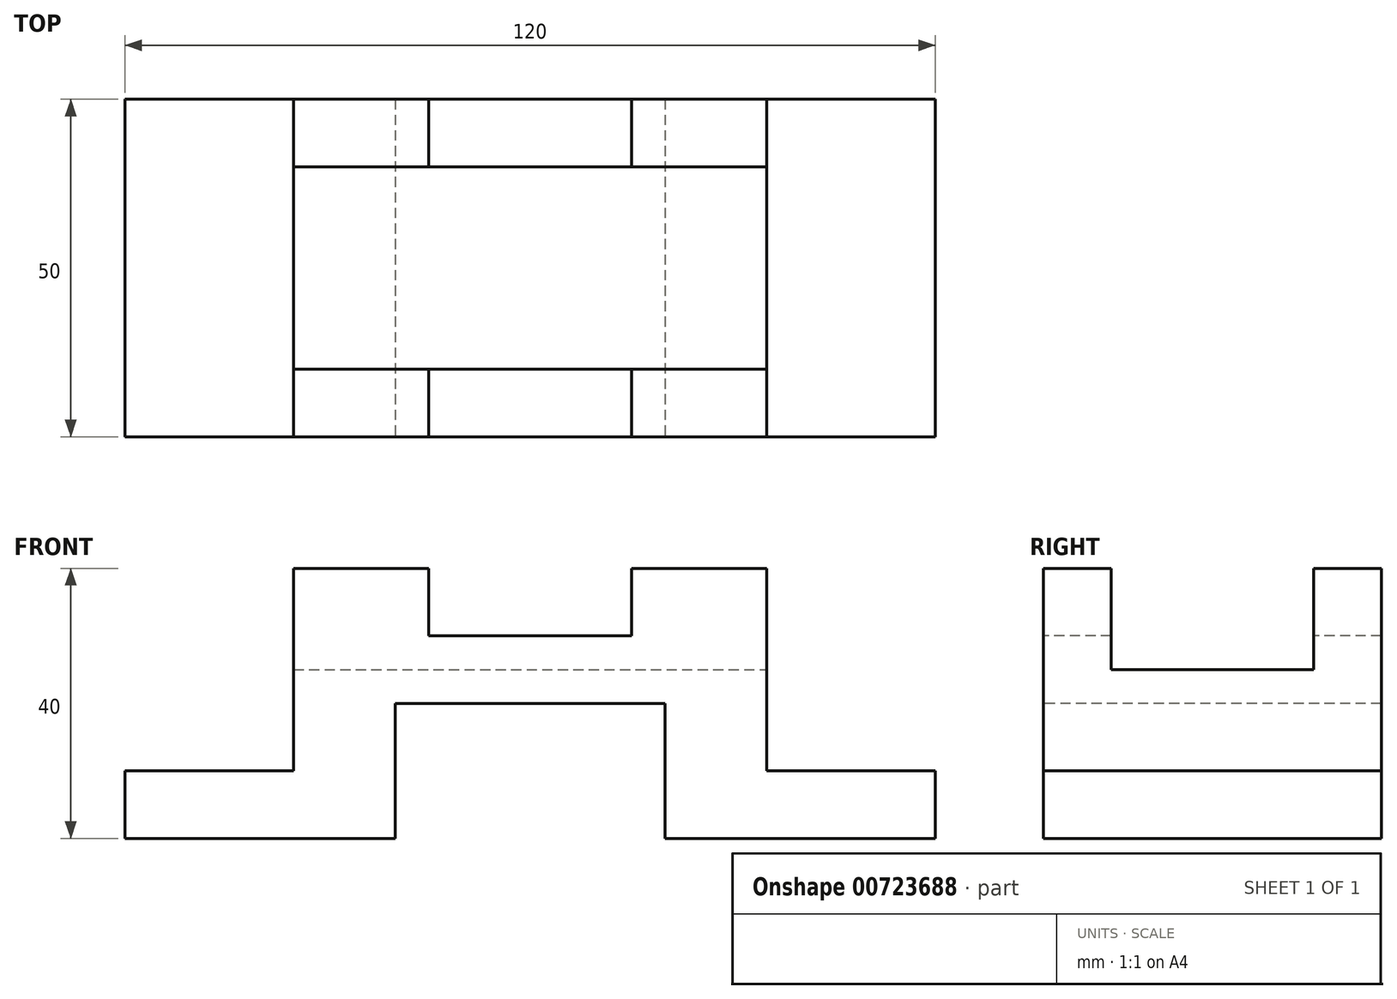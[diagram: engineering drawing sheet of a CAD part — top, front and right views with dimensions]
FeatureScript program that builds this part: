
annotation { "Feature Type Name" : "Feature", "Feature Type Description" : "" }
export const myFeature = defineFeature(function(context is Context, id is Id, definition is map)
    precondition{}
    {
        {
            var Q0;
            Q0=qCreatedBy(makeId("Front.planeOp"),FACE);
            var sketch = newSketch(context, id + "F0", { "sketchPlane" : qUnion([Q0])});
            skLineSegment(sketch, "E0", {"start": v(0, 0) * mm, "end": v(-40, 0) * mm});
            skLineSegment(sketch, "E1", {"start": v(-40, 0) * mm, "end": v(-40, 20) * mm});
            skLineSegment(sketch, "E2", {"start": v(-40, 20) * mm, "end": v(-80, 20) * mm});
            skLineSegment(sketch, "E3", {"start": v(-80, 20) * mm, "end": v(-80, 0) * mm});
            skLineSegment(sketch, "E4", {"start": v(-80, 0) * mm, "end": v(-120, 0) * mm});
            skLineSegment(sketch, "E5", {"start": v(-120, 0) * mm, "end": v(-120, 10) * mm});
            skLineSegment(sketch, "E6", {"start": v(-120, 10) * mm, "end": v(-95, 10) * mm});
            skLineSegment(sketch, "E7", {"start": v(-95, 10) * mm, "end": v(-95, 40) * mm});
            skLineSegment(sketch, "E8", {"start": v(-95, 40) * mm, "end": v(-75, 40) * mm});
            skLineSegment(sketch, "E9", {"start": v(-75, 40) * mm, "end": v(-75, 30) * mm});
            skLineSegment(sketch, "E10", {"start": v(-75, 30) * mm, "end": v(-45, 30) * mm});
            skLineSegment(sketch, "E11", {"start": v(-45, 30) * mm, "end": v(-45, 40) * mm});
            skLineSegment(sketch, "E12", {"start": v(-45, 40) * mm, "end": v(-25, 40) * mm});
            skLineSegment(sketch, "E13", {"start": v(-25, 40) * mm, "end": v(-25, 10) * mm});
            skLineSegment(sketch, "E14", {"start": v(-25, 10) * mm, "end": v(0, 10) * mm});
            skLineSegment(sketch, "E15", {"start": v(0, 10) * mm, "end": v(0, 0) * mm});
            skSolve(sketch);
        }
        {
            var Q0;
            Q0 = qSketchRegion(id + "F0", true);
            extrude(context, id + "F1", {"entities" : qUnion([Q0]), "oppositeDirection" : true, "depth" : 50 * mm, "offsetDistance" : 25 * mm});
        }
        {
            var Q0;
            Q0=makeQuery(id+"F1.opExtrude","SWEPT_FACE",FACE,{"disambiguationData":[OSD([sQuery(id+"F0.wireOp",EDGE,"E13")])]});
            var sketch = newSketch(context, id + "F2", { "sketchPlane" : qUnion([Q0])});
            skLineSegment(sketch, "E16.bottom", {"start": v(10, 25) * mm, "end": v(40, 25) * mm});
            skLineSegment(sketch, "E16.top", {"start": v(10, 55) * mm, "end": v(40, 55) * mm});
            skLineSegment(sketch, "E16.left", {"start": v(10, 25) * mm, "end": v(10, 55) * mm});
            skLineSegment(sketch, "E16.right", {"start": v(40, 25) * mm, "end": v(40, 55) * mm});
            skPoint(sketch, "E16.middle", {"position": v(25, 40) * mm});
            skSolve(sketch);
        }
        {
            var Q0;
            Q0 = qSketchRegion(id + "F2", true);
            extrude(context, id + "F3", {"entities" : qUnion([Q0]), "operationType" : NewBodyOperationType.REMOVE, "oppositeDirection" : true, "depth" : 70 * mm, "offsetDistance" : 25 * mm});
        }
    });
